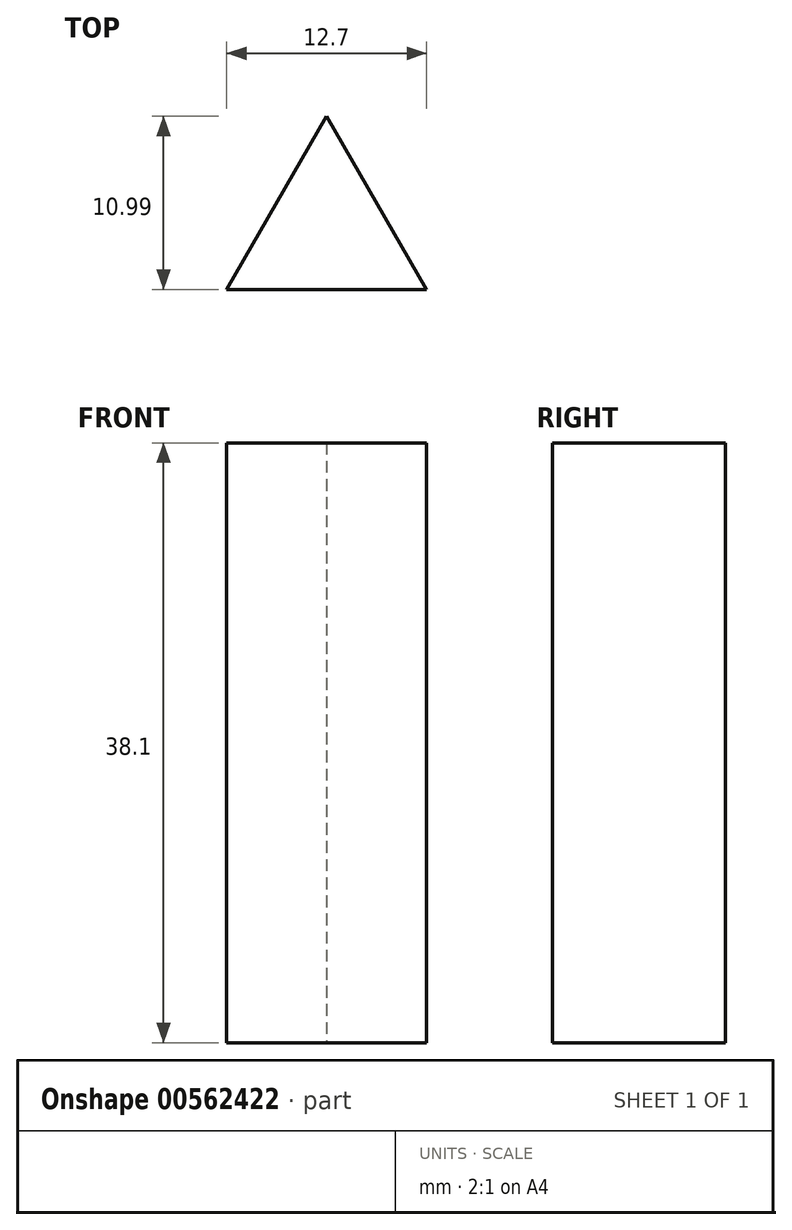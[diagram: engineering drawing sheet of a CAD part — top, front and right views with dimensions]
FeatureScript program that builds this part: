
annotation { "Feature Type Name" : "Feature", "Feature Type Description" : "" }
export const myFeature = defineFeature(function(context is Context, id is Id, definition is map)
    precondition{}
    {
        {
            var Q0;
            Q0=qCreatedBy(makeId("Top.planeOp"),FACE);
            var sketch = newSketch(context, id + "F0", { "sketchPlane" : qUnion([Q0])});
            skLineSegment(sketch, "E0", {"start": v(0, 6.21) * mm, "end": v(-6.35, -4.78) * mm});
            skLineSegment(sketch, "E1", {"start": v(-6.35, -4.78) * mm, "end": v(6.35, -4.78) * mm});
            skLineSegment(sketch, "E2", {"start": v(6.35, -4.78) * mm, "end": v(0, 6.21) * mm});
            skSolve(sketch);
        }
        {
            var Q0;
            Q0 = qSketchRegion(id + "F0", true);
            extrude(context, id + "F1", {"entities" : qUnion([Q0]), "depth" : 38.1 * mm, "offsetDistance" : 25.4 * mm});
        }
    });
